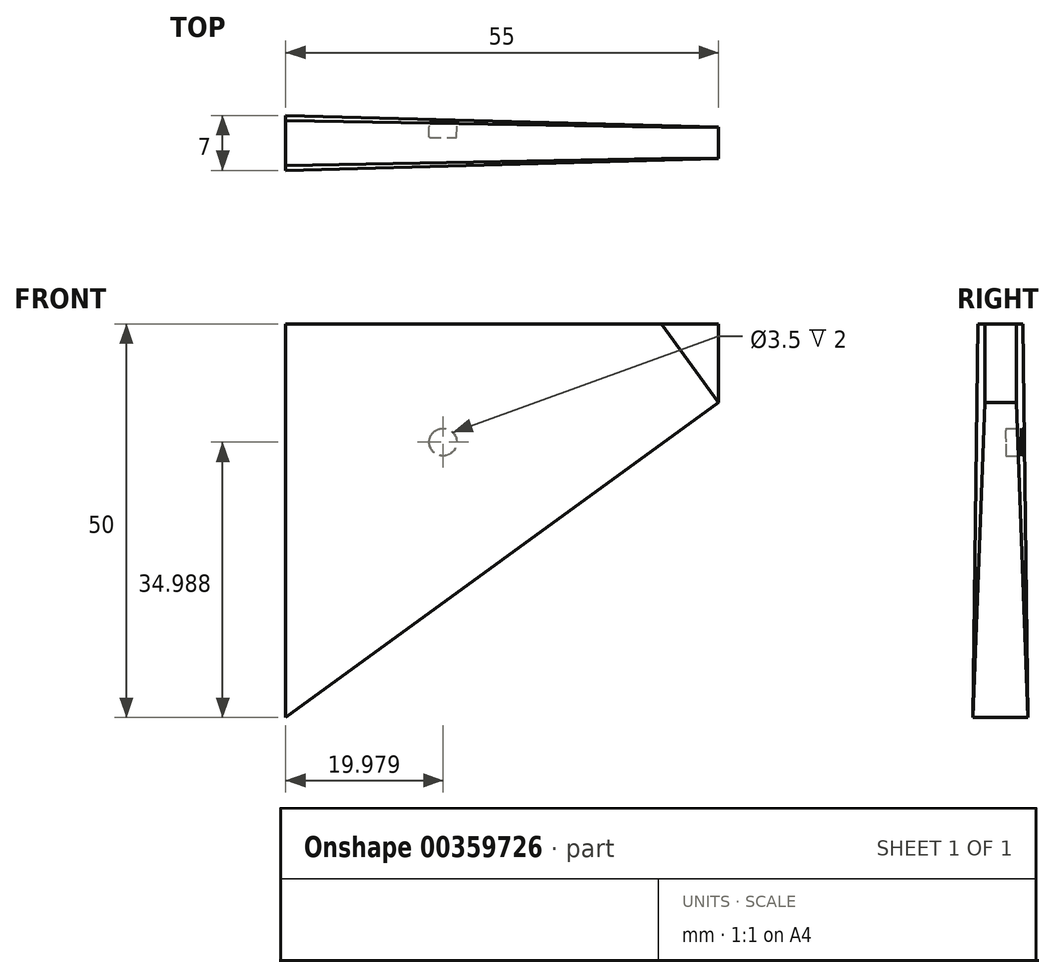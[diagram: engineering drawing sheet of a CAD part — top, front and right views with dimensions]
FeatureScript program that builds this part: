
annotation { "Feature Type Name" : "Feature", "Feature Type Description" : "" }
export const myFeature = defineFeature(function(context is Context, id is Id, definition is map)
    precondition{}
    {
        {
            var Q0;
            Q0=qCreatedBy(makeId("Front.planeOp"),FACE);
            var sketch = newSketch(context, id + "F0", { "sketchPlane" : qUnion([Q0])});
            skLineSegment(sketch, "E0.bottom", {"start": v(27.5, 25) * mm, "end": v(-27.5, 25) * mm});
            skLineSegment(sketch, "E0.top", {"start": v(27.5, -25) * mm, "end": v(-27.5, -25) * mm});
            skLineSegment(sketch, "E0.left", {"start": v(27.5, 25) * mm, "end": v(27.5, -25) * mm});
            skLineSegment(sketch, "E0.right", {"start": v(-27.5, 25) * mm, "end": v(-27.5, -25) * mm});
            skPoint(sketch, "E0.middle", {"position": v(0, 0) * mm});
            skLineSegment(sketch, "E1", {"start": v(-27.5, -25) * mm, "end": v(27.5, 15) * mm});
            skSolve(sketch);
        }
        {
            var Q0;
            {var subQ0=sQuery(id+"F0.wireOp",EDGE,"E0.bottom");Q0=makeQuery(id+"F0.imprint","IMPRINT",FACE,{"disambiguationData":[TD([[makeQuery(id+"F0.imprint","IMPRINT",EDGE,{"derivedFrom":subQ0}),1.0]])]});}
            extrude(context, id + "F1", {"entities" : qUnion([Q0]), "depth" : 7 * mm});
        }
        {
            var Q0;
            Q0=makeQuery(id+"F1.opExtrude","SWEPT_FACE",FACE,{"disambiguationData":[OSD([sQuery(id+"F0.wireOp",EDGE,"E1")])]});
            var sketch = newSketch(context, id + "F2", { "sketchPlane" : qUnion([Q0])});
            skLineSegment(sketch, "E2", {"start": v(-36.94, 0) * mm, "end": v(31.06, 1.5) * mm});
            skLineSegment(sketch, "E3", {"start": v(-36.94, 7) * mm, "end": v(31.06, 5.5) * mm});
            skSolve(sketch);
        }
        {
            var Q0;
            {var subQ0=sQuery(id+"F2.wireOp",EDGE,"E3");Q0=makeQuery(id+"F2.imprint","IMPRINT",FACE,{"disambiguationData":[TD([[makeQuery(id+"F2.imprint","IMPRINT",EDGE,{"derivedFrom":subQ0}),1.0]])]});}
            var Q1;
            {var subQ0=sQuery(id+"F2.wireOp",EDGE,"E2");Q1=makeQuery(id+"F2.imprint","IMPRINT",FACE,{"disambiguationData":[TD([[makeQuery(id+"F2.imprint","IMPRINT",EDGE,{"derivedFrom":subQ0}),-1.0]])]});}
            extrude(context, id + "F3", {"entities" : qUnion([Q0, Q1]), "operationType" : NewBodyOperationType.REMOVE, "endBound" : BoundingType.THROUGH_ALL, "oppositeDirection" : true, "depth" : 25 * mm});
        }
        {
            var Q0;
            {var subQ0=sQuery(id+"F0.wireOp",EDGE,"E1");var subQ1=sQuery(id+"F0.wireOp",EDGE,"E0.left");var subQ2=makeQuery(id+"F1.opExtrude","SWEPT_EDGE",EDGE,{"disambiguationData":[OSD([subQ1,subQ0])]});Q0=makeQuery(id+"F3.boolean.opBoolean","COPY",FACE,{"derivedFrom":makeQuery(id+"F3.opExtrude","SWEPT_FACE",FACE,{"disambiguationData":[OSD([subQ1,subQ0]),TDD([makeQuery(id+"F2.imprint","IMPRINT",EDGE,{"disambiguationData":[TD([[makeQuery(id+"F2.imprint","INTERSECT",VERTEX,{"derivedFrom":[subQ2,makeQuery(id+"F1.opExtrude","CAP_EDGE",EDGE,{"disambiguationData":[OSD([subQ0])],"isStart":false})]}),-1.0]])],"derivedFrom":subQ2})])]})});}
            var Q1;
            {var subQ0=sQuery(id+"F0.wireOp",EDGE,"E1");var subQ1=sQuery(id+"F0.wireOp",EDGE,"E0.left");var subQ2=makeQuery(id+"F1.opExtrude","SWEPT_EDGE",EDGE,{"disambiguationData":[OSD([subQ1,subQ0])]});Q1=makeQuery(id+"F3.boolean.opBoolean","COPY",FACE,{"derivedFrom":makeQuery(id+"F3.opExtrude","SWEPT_FACE",FACE,{"disambiguationData":[OSD([subQ1,subQ0]),TDD([makeQuery(id+"F2.imprint","IMPRINT",EDGE,{"disambiguationData":[TD([[makeQuery(id+"F2.imprint","INTERSECT",VERTEX,{"derivedFrom":[subQ2,makeQuery(id+"F1.opExtrude","CAP_EDGE",EDGE,{"disambiguationData":[OSD([subQ0])],"isStart":true})]}),1.0]])],"derivedFrom":subQ2})])]})});}
            extrude(context, id + "F4", {"entities" : qUnion([Q0, Q1]), "operationType" : NewBodyOperationType.REMOVE, "endBound" : BoundingType.THROUGH_ALL, "oppositeDirection" : true, "depth" : 25 * mm});
        }
        {
            var Q0;
            Q0=makeQuery(id+"F3.boolean.opBoolean","COPY",FACE,{"derivedFrom":makeQuery(id+"F3.opExtrude","SWEPT_FACE",FACE,{"disambiguationData":[OSD([sQuery(id+"F2.wireOp",EDGE,"E2")])]})});
            var sketch = newSketch(context, id + "F5", { "sketchPlane" : qUnion([Q0])});
            skCircle(sketch, "E4", {"center": v(7.49, 10.01) * mm, "radius": 1.75 * mm});
            skSolve(sketch);
        }
        {
            var Q0;
            Q0=makeQuery(id+"F5.imprint","IMPRINT",FACE,{"disambiguationData":[TD([[makeQuery(id+"F5.imprint","IMPRINT",EDGE,{"derivedFrom":sQuery(id+"F5.wireOp",EDGE,"E4")}),1.0]])]});
            extrude(context, id + "F6", {"entities" : qUnion([Q0]), "operationType" : NewBodyOperationType.REMOVE, "oppositeDirection" : true, "depth" : 2 * mm});
        }
    });
